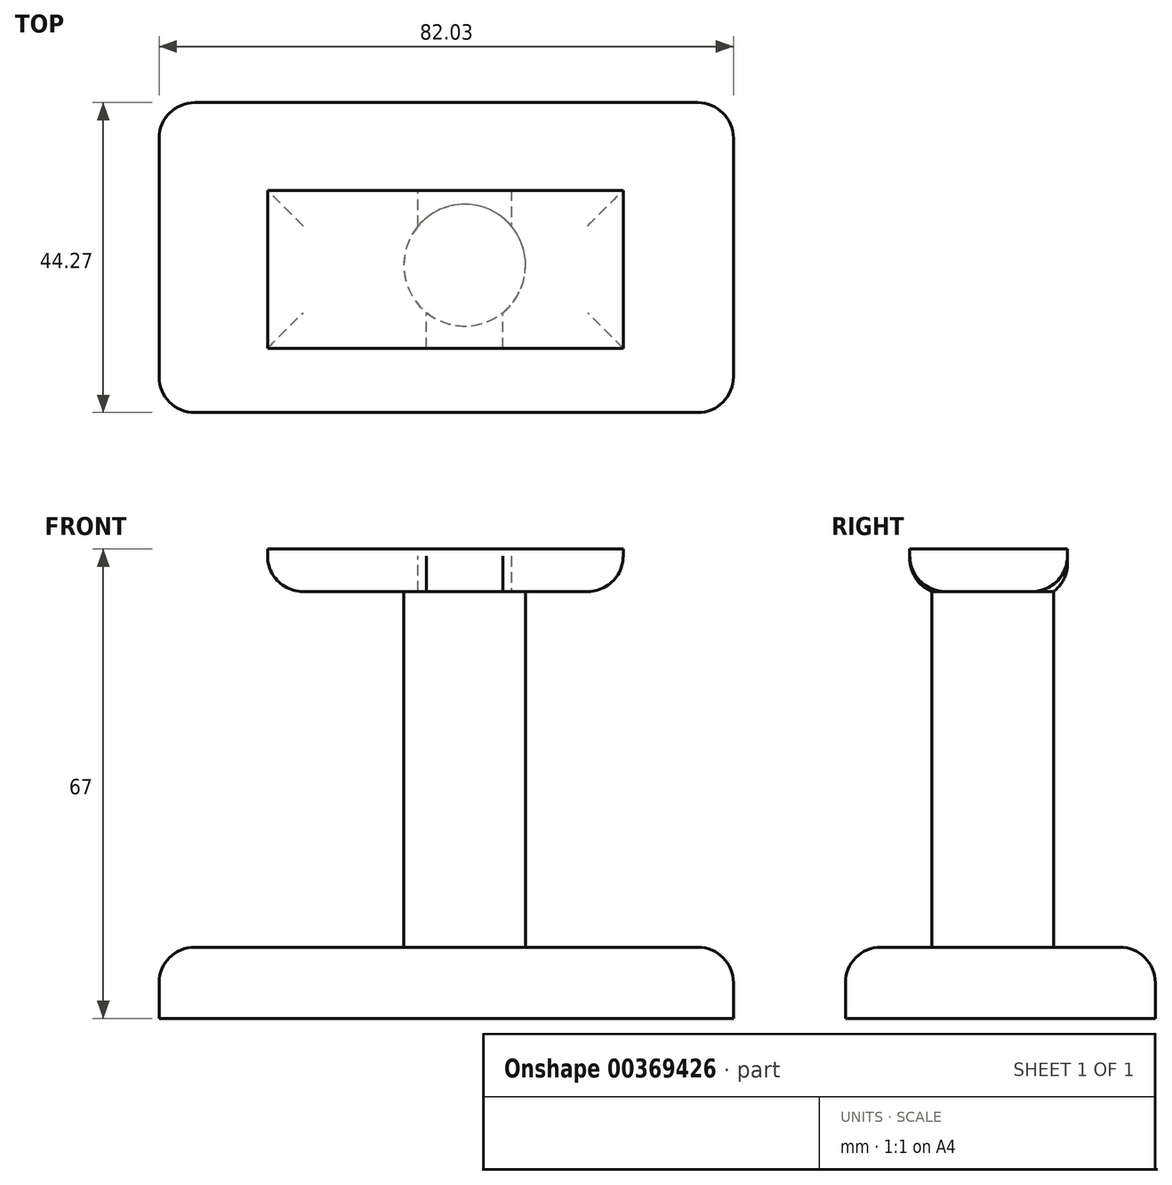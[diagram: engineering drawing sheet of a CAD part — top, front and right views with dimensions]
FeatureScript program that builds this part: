
annotation { "Feature Type Name" : "Feature", "Feature Type Description" : "" }
export const myFeature = defineFeature(function(context is Context, id is Id, definition is map)
    precondition{}
    {
        {
            var Q0;
            Q0=qCreatedBy(makeId("Top.planeOp"),FACE);
            var sketch = newSketch(context, id + "F0", { "sketchPlane" : qUnion([Q0])});
            skLineSegment(sketch, "E0.bottom", {"start": v(-15.48, 19.04) * mm, "end": v(66.55, 19.04) * mm});
            skLineSegment(sketch, "E0.top", {"start": v(-15.48, -25.23) * mm, "end": v(66.55, -25.23) * mm});
            skLineSegment(sketch, "E0.left", {"start": v(-15.48, 19.04) * mm, "end": v(-15.48, -25.23) * mm});
            skLineSegment(sketch, "E0.right", {"start": v(66.55, 19.04) * mm, "end": v(66.55, -25.23) * mm});
            skSolve(sketch);
        }
        {
            var Q0;
            Q0=makeQuery(id+"F0.imprint","IMPRINT",FACE,{"disambiguationData":[TD([[makeQuery(id+"F0.imprint","IMPRINT",EDGE,{"derivedFrom":sQuery(id+"F0.wireOp",EDGE,"E0.bottom")}),-1.0]])]});
            extrude(context, id + "F1", {"entities" : qUnion([Q0]), "oppositeDirection" : true, "depth" : 10.16 * mm});
        }
        {
            var Q0;
            Q0=qCreatedBy(makeId("Top.planeOp"),FACE);
            var sketch = newSketch(context, id + "F2", { "sketchPlane" : qUnion([Q0])});
            skCircle(sketch, "E1", {"center": v(28.17, -4.18) * mm, "radius": 8.69 * mm});
            skSolve(sketch);
        }
        {
            var Q0;
            Q0=makeQuery(id+"F2.imprint","IMPRINT",FACE,{"disambiguationData":[TD([[makeQuery(id+"F2.imprint","IMPRINT",EDGE,{"derivedFrom":sQuery(id+"F2.wireOp",EDGE,"E1")}),1.0]])]});
            extrude(context, id + "F3", {"entities" : qUnion([Q0]), "operationType" : NewBodyOperationType.ADD, "depth" : 50.8 * mm});
        }
        {
            var Q0;
            Q0=makeQuery(id+"F1.opExtrude","SWEPT_EDGE",EDGE,{"disambiguationData":[OSD([sQuery(id+"F0.wireOp",EDGE,"E0.top"),sQuery(id+"F0.wireOp",EDGE,"E0.left")])]});
            var Q1;
            Q1=makeQuery(id+"F1.opExtrude","SWEPT_EDGE",EDGE,{"disambiguationData":[OSD([sQuery(id+"F0.wireOp",EDGE,"E0.top"),sQuery(id+"F0.wireOp",EDGE,"E0.right")])]});
            var Q2;
            Q2=makeQuery(id+"F1.opExtrude","SWEPT_EDGE",EDGE,{"disambiguationData":[OSD([sQuery(id+"F0.wireOp",EDGE,"E0.bottom"),sQuery(id+"F0.wireOp",EDGE,"E0.left")])]});
            var Q3;
            Q3=makeQuery(id+"F1.opExtrude","SWEPT_EDGE",EDGE,{"disambiguationData":[OSD([sQuery(id+"F0.wireOp",EDGE,"E0.bottom"),sQuery(id+"F0.wireOp",EDGE,"E0.right")])]});
            fillet(context, id + "F4", {"entities" : qUnion([Q0, Q1, Q2, Q3]), "radius" : 5.08 * mm, "tangentPropagation" : true, "allowEdgeOverflow" : false});
        }
        {
            var Q0;
            Q0=makeQuery(id+"F1.opExtrude","CAP_EDGE",EDGE,{"disambiguationData":[OSD([sQuery(id+"F0.wireOp",EDGE,"E0.top")])],"isStart":true});
            var Q1;
            Q1=makeQuery(id+"F1.opExtrude","CAP_EDGE",EDGE,{"disambiguationData":[OSD([sQuery(id+"F0.wireOp",EDGE,"E0.right")])],"isStart":true});
            var Q2;
            Q2=makeQuery(id+"F1.opExtrude","CAP_EDGE",EDGE,{"disambiguationData":[OSD([sQuery(id+"F0.wireOp",EDGE,"E0.left")])],"isStart":true});
            fillet(context, id + "F5", {"entities" : qUnion([Q0, Q1, Q2]), "radius" : 5.08 * mm, "tangentPropagation" : true, "allowEdgeOverflow" : false});
        }
        {
            var Q0;
            Q0=qCreatedBy(makeId("Right.planeOp"),FACE);
            var sketch = newSketch(context, id + "F6", { "sketchPlane" : qUnion([Q0])});
            skLineSegment(sketch, "E2.bottom", {"start": v(6.5, 56.84) * mm, "end": v(-16.03, 56.84) * mm});
            skLineSegment(sketch, "E2.top", {"start": v(6.5, 50.78) * mm, "end": v(-16.03, 50.78) * mm});
            skLineSegment(sketch, "E2.left", {"start": v(6.5, 56.84) * mm, "end": v(6.5, 50.78) * mm});
            skLineSegment(sketch, "E2.right", {"start": v(-16.03, 56.84) * mm, "end": v(-16.03, 50.78) * mm});
            skSolve(sketch);
        }
        {
            var Q0;
            Q0 = qSketchRegion(id + "F6", true);
            extrude(context, id + "F7", {"entities" : qUnion([Q0]), "operationType" : NewBodyOperationType.ADD, "depth" : 50.8 * mm});
        }
        {
            var Q0;
            Q0=makeQuery(id+"F7.opExtrude","SWEPT_EDGE",EDGE,{"disambiguationData":[OSD([sQuery(id+"F6.wireOp",EDGE,"E2.top"),sQuery(id+"F6.wireOp",EDGE,"E2.right")])]});
            var Q1;
            Q1=makeQuery(id+"F7.opExtrude","CAP_EDGE",EDGE,{"disambiguationData":[OSD([sQuery(id+"F6.wireOp",EDGE,"E2.top")])],"isStart":false});
            var Q2;
            Q2=makeQuery(id+"F7.opExtrude","CAP_EDGE",EDGE,{"disambiguationData":[OSD([sQuery(id+"F6.wireOp",EDGE,"E2.top")])],"isStart":true});
            var Q3;
            Q3=makeQuery(id+"F7.opExtrude","SWEPT_EDGE",EDGE,{"disambiguationData":[OSD([sQuery(id+"F6.wireOp",EDGE,"E2.top"),sQuery(id+"F6.wireOp",EDGE,"E2.left")])]});
            fillet(context, id + "F8", {"entities" : qUnion([Q0, Q1, Q2, Q3]), "radius" : 5.08 * mm, "tangentPropagation" : true, "allowEdgeOverflow" : false});
        }
    });
